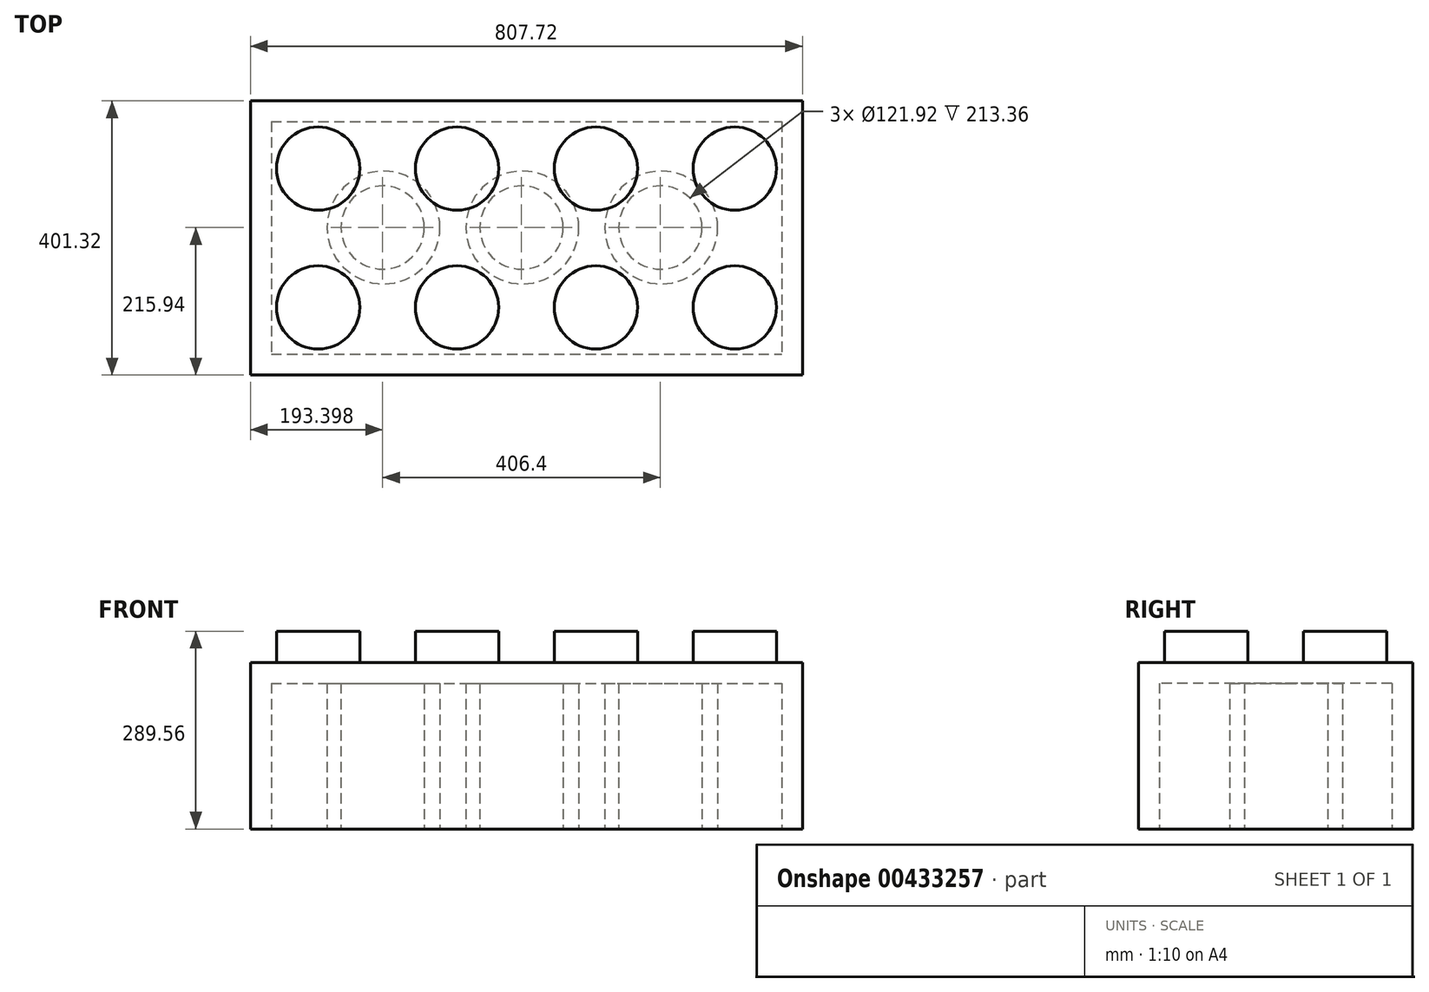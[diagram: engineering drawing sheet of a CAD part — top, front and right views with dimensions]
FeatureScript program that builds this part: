
annotation { "Feature Type Name" : "Feature", "Feature Type Description" : "" }
export const myFeature = defineFeature(function(context is Context, id is Id, definition is map)
    precondition{}
    {
        {
            var Q0;
            Q0=qCreatedBy(makeId("Top.planeOp"),FACE);
            var sketch = newSketch(context, id + "F0", { "sketchPlane" : qUnion([Q0])});
            skLineSegment(sketch, "E0.bottom", {"start": v(-434.65, 185.38) * mm, "end": v(373.07, 185.38) * mm});
            skLineSegment(sketch, "E0.top", {"start": v(-434.65, -215.94) * mm, "end": v(373.07, -215.94) * mm});
            skLineSegment(sketch, "E0.left", {"start": v(-434.65, 185.38) * mm, "end": v(-434.65, -215.94) * mm});
            skLineSegment(sketch, "E0.right", {"start": v(373.07, 185.38) * mm, "end": v(373.07, -215.94) * mm});
            skSolve(sketch);
        }
        {
            var Q0;
            Q0 = qSketchRegion(id + "F0", true);
            extrude(context, id + "F1", {"entities" : qUnion([Q0]), "depth" : 243.84 * mm});
        }
        {
            var Q0;
            Q0=makeQuery(id+"F1.opExtrude","CAP_FACE",FACE,{"disambiguationData":[OSD([sQuery(id+"F0.wireOp",EDGE,"E0.bottom"),sQuery(id+"F0.wireOp",EDGE,"E0.top"),sQuery(id+"F0.wireOp",EDGE,"E0.left"),sQuery(id+"F0.wireOp",EDGE,"E0.right")])],"isStart":false});
            var sketch = newSketch(context, id + "F2", { "sketchPlane" : qUnion([Q0])});
            skCircle(sketch, "E1", {"center": v(-335.59, 86.32) * mm, "radius": 60.96 * mm});
            skCircle(sketch, "E2.0.1.0", {"center": v(-335.59, -116.88) * mm, "radius": 60.96 * mm});
            skCircle(sketch, "E2.1.0.0", {"center": v(-132.39, 86.32) * mm, "radius": 60.96 * mm});
            skCircle(sketch, "E2.1.1.0", {"center": v(-132.39, -116.88) * mm, "radius": 60.96 * mm});
            skCircle(sketch, "E2.2.0.0", {"center": v(70.81, 86.32) * mm, "radius": 60.96 * mm});
            skCircle(sketch, "E2.2.1.0", {"center": v(70.81, -116.88) * mm, "radius": 60.96 * mm});
            skCircle(sketch, "E2.3.0.0", {"center": v(274.01, 86.32) * mm, "radius": 60.96 * mm});
            skCircle(sketch, "E2.3.1.0", {"center": v(274.01, -116.88) * mm, "radius": 60.96 * mm});
            skLineSegment(sketch, "E2.direction1", {"start": v(-335.59, 86.32) * mm, "end": v(-132.39, 86.32) * mm, "construction": true});
            skLineSegment(sketch, "E2.direction2", {"start": v(-335.59, 86.32) * mm, "end": v(-335.59, -116.88) * mm, "construction": true});
            skSolve(sketch);
        }
        {
            var Q0;
            Q0=makeQuery(id+"F2.imprint","IMPRINT",FACE,{"disambiguationData":[TD([[makeQuery(id+"F2.imprint","IMPRINT",EDGE,{"derivedFrom":sQuery(id+"F2.wireOp",EDGE,"E2.0.1.0")}),1.0]])]});
            var Q1;
            Q1=makeQuery(id+"F2.imprint","IMPRINT",FACE,{"disambiguationData":[TD([[makeQuery(id+"F2.imprint","IMPRINT",EDGE,{"derivedFrom":sQuery(id+"F2.wireOp",EDGE,"E2.1.0.0")}),1.0]])]});
            var Q2;
            Q2=makeQuery(id+"F2.imprint","IMPRINT",FACE,{"disambiguationData":[TD([[makeQuery(id+"F2.imprint","IMPRINT",EDGE,{"derivedFrom":sQuery(id+"F2.wireOp",EDGE,"E2.1.1.0")}),1.0]])]});
            var Q3;
            Q3=makeQuery(id+"F2.imprint","IMPRINT",FACE,{"disambiguationData":[TD([[makeQuery(id+"F2.imprint","IMPRINT",EDGE,{"derivedFrom":sQuery(id+"F2.wireOp",EDGE,"E2.2.0.0")}),1.0]])]});
            var Q4;
            Q4=makeQuery(id+"F2.imprint","IMPRINT",FACE,{"disambiguationData":[TD([[makeQuery(id+"F2.imprint","IMPRINT",EDGE,{"derivedFrom":sQuery(id+"F2.wireOp",EDGE,"E2.3.1.0")}),1.0]])]});
            var Q5;
            Q5=makeQuery(id+"F2.imprint","IMPRINT",FACE,{"disambiguationData":[TD([[makeQuery(id+"F2.imprint","IMPRINT",EDGE,{"derivedFrom":sQuery(id+"F2.wireOp",EDGE,"E2.2.1.0")}),1.0]])]});
            var Q6;
            Q6=makeQuery(id+"F2.imprint","IMPRINT",FACE,{"disambiguationData":[TD([[makeQuery(id+"F2.imprint","IMPRINT",EDGE,{"derivedFrom":sQuery(id+"F2.wireOp",EDGE,"E2.3.0.0")}),1.0]])]});
            var Q7;
            Q7=makeQuery(id+"F2.imprint","IMPRINT",FACE,{"disambiguationData":[TD([[makeQuery(id+"F2.imprint","IMPRINT",EDGE,{"derivedFrom":sQuery(id+"F2.wireOp",EDGE,"E1")}),1.0]])]});
            extrude(context, id + "F3", {"entities" : qUnion([Q0, Q1, Q2, Q3, Q4, Q5, Q6, Q7]), "operationType" : NewBodyOperationType.ADD, "depth" : 45.72 * mm});
        }
        {
            var Q0;
            Q0=makeQuery(id+"F1.opExtrude","CAP_FACE",FACE,{"disambiguationData":[OSD([sQuery(id+"F0.wireOp",EDGE,"E0.bottom"),sQuery(id+"F0.wireOp",EDGE,"E0.top"),sQuery(id+"F0.wireOp",EDGE,"E0.left"),sQuery(id+"F0.wireOp",EDGE,"E0.right")])],"isStart":true});
            var sketch = newSketch(context, id + "F4", { "sketchPlane" : qUnion([Q0])});
            skCircle(sketch, "E3", {"center": v(166.4, 0) * mm, "radius": 82.55 * mm});
            skCircle(sketch, "E4.1.0.0", {"center": v(-36.8, 0) * mm, "radius": 82.55 * mm});
            skCircle(sketch, "E4.2.0.0", {"center": v(-240, 0) * mm, "radius": 82.55 * mm});
            skLineSegment(sketch, "E4.direction1", {"start": v(166.4, 0) * mm, "end": v(-36.8, 0) * mm, "construction": true});
            skSolve(sketch);
        }
        {
            var Q0;
            Q0=makeQuery(id+"F4.imprint","IMPRINT",FACE,{"disambiguationData":[TD([[makeQuery(id+"F4.imprint","IMPRINT",EDGE,{"derivedFrom":sQuery(id+"F4.wireOp",EDGE,"E3")}),-1.0]])]});
            var sketch = newSketch(context, id + "F5", { "sketchPlane" : qUnion([Q0])});
            skCircle(sketch, "E5", {"center": v(165.15, 0) * mm, "radius": 60.96 * mm});
            skCircle(sketch, "E6.1.0.0", {"center": v(-38.05, 0) * mm, "radius": 60.96 * mm});
            skCircle(sketch, "E6.2.0.0", {"center": v(-241.25, 0) * mm, "radius": 60.96 * mm});
            skLineSegment(sketch, "E6.direction1", {"start": v(165.15, 0) * mm, "end": v(-38.05, 0) * mm, "construction": true});
            skSolve(sketch);
        }
        {
            var Q0;
            Q0=makeQuery(id+"F4.imprint","IMPRINT",FACE,{"disambiguationData":[TD([[makeQuery(id+"F4.imprint","IMPRINT",EDGE,{"derivedFrom":sQuery(id+"F4.wireOp",EDGE,"E3")}),-1.0]])]});
            var sketch = newSketch(context, id + "F6", { "sketchPlane" : qUnion([Q0])});
            skLineSegment(sketch, "E7.bottom", {"start": v(-404.17, -154.9) * mm, "end": v(342.6, -154.9) * mm});
            skLineSegment(sketch, "E7.top", {"start": v(-404.17, 185.46) * mm, "end": v(342.6, 185.46) * mm});
            skLineSegment(sketch, "E7.left", {"start": v(-404.17, -154.9) * mm, "end": v(-404.17, 185.46) * mm});
            skLineSegment(sketch, "E7.right", {"start": v(342.6, -154.9) * mm, "end": v(342.6, 185.46) * mm});
            skSolve(sketch);
        }
        {
            var Q0;
            Q0=makeQuery(id+"F6.imprint","IMPRINT",FACE,{"disambiguationData":[TD([[makeQuery(id+"F6.imprint","IMPRINT",EDGE,{"derivedFrom":sQuery(id+"F6.wireOp",EDGE,"E7.bottom")}),1.0]])]});
            extrude(context, id + "F7", {"entities" : qUnion([Q0]), "operationType" : NewBodyOperationType.REMOVE, "oppositeDirection" : true, "depth" : 213.36 * mm});
        }
        {
            var Q0;
            Q0 = qSketchRegion(id + "F5", true);
            extrude(context, id + "F8", {"entities" : qUnion([Q0]), "operationType" : NewBodyOperationType.REMOVE, "oppositeDirection" : true, "depth" : 213.36 * mm});
        }
    });
